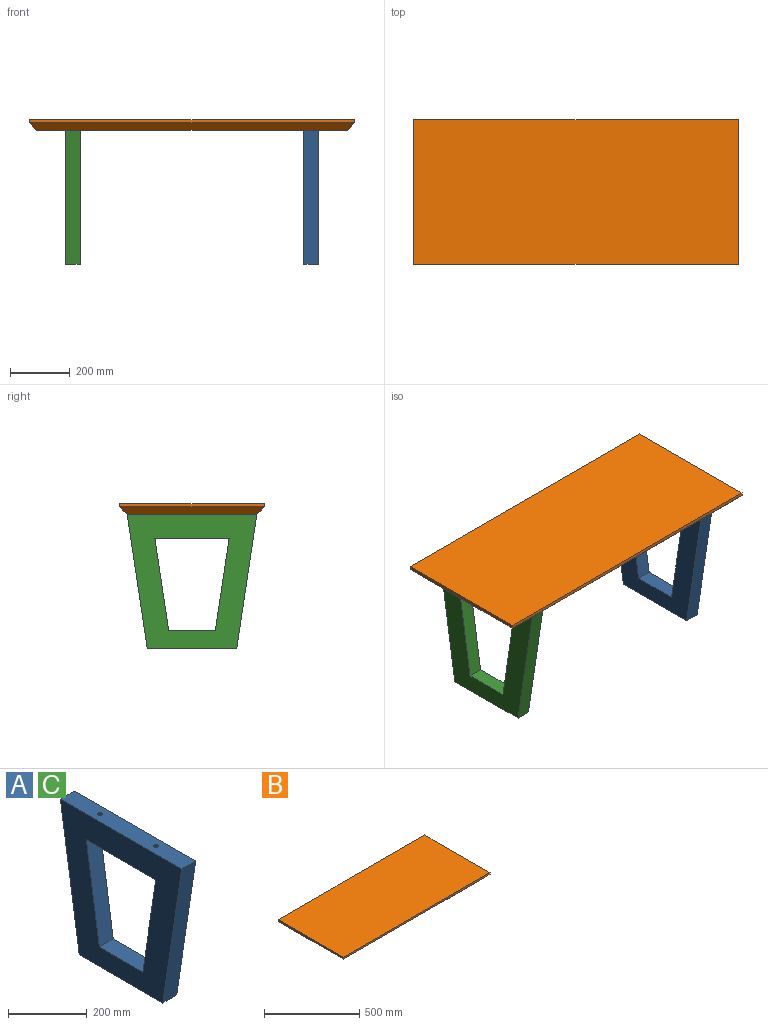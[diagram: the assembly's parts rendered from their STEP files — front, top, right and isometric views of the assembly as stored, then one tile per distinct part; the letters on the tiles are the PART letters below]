
ASSEMBLY  parts=3 mates=2
PART A: 16 faces, bbox 50x435x450 mm
  f0: cylinder r=6mm len=60mm, axis (0,0,-1), area 2261.9mm2, adj f5,f15
  f1: cylinder r=6mm len=60mm, axis (0,0,-1), area 2261.9mm2, adj f5,f13
  f2: plane 310x50mm, normal (0,0.99,0.15), area 15673.4mm2, adj f3,f9,f10,f11
  f3: plane 249.21x50mm, normal (0,0,-1), area 10536.3mm2, adj f2,f4,f10,f11,f12,f14
  f4: plane 310x50mm, normal (0,-0.99,0.15), area 15673.4mm2, adj f3,f9,f10,f11
  f5: plane 435x50mm, normal (0,0,1), area 21523.8mm2, adj f0,f1,f6,f8,f10,f11
  f6: plane 450x67.5mm, normal (0,-0.99,-0.15), area 22751.7mm2, adj f5,f7,f10,f11
  f7: plane 300x50mm, normal (0,0,-1), area 15000mm2, adj f6,f8,f10,f11
  f8: plane 450x67.5mm, normal (0,0.99,-0.15), area 22751.7mm2, adj f5,f7,f10,f11
  f9: plane 156.21x50mm, normal (0,0,1), area 7810.5mm2, adj f2,f4,f10,f11
  f10: plane 450x435mm, normal (1,0,0), area 102534.9mm2, adj f2,f3,f4,f5,f6,f7,f8,f9
  f11: plane 450x435mm, normal (-1,0,0), area 102534.9mm2, adj f2,f3,f4,f5,f6,f7,f8,f9
  f12: cylinder r=17.5mm len=35mm, axis (0,0,-1), area 2199.1mm2, adj f3,f13
  f13: plane 35x35mm, normal (0,0,-1), area 849mm2, adj f1,f12
  f14: cylinder r=17.5mm len=35mm, axis (0,0,-1), area 2199.1mm2, adj f3,f15
  f15: plane 35x35mm, normal (0,0,-1), area 849mm2, adj f0,f14
PART B: 10 faces, bbox 1090x485x36 mm
  f0: plane 485x11mm, normal (1,0,0), area 5335mm2, adj f1,f3,f4,f6
  f1: plane 1090x11mm, normal (0,1,0), area 11990mm2, adj f0,f2,f4,f7
  f2: plane 485x11mm, normal (-1,0,0), area 5335mm2, adj f1,f3,f4,f9
  f3: plane 1090x11mm, normal (0,-1,0), area 11990mm2, adj f0,f2,f4,f8
  f4: plane 1090x485mm, normal (0,0,1), area 528650mm2, adj f0,f1,f2,f3
  f5: plane 1040x435mm, normal (0,0,-1), area 452400mm2, adj f6,f7,f8,f9
  f6: plane 485x25mm, normal (0.71,0,-0.71), area 16263.5mm2, adj f0,f5,f7,f8
  f7: plane 1090x25mm, normal (0,0.71,-0.71), area 37653.4mm2, adj f1,f5,f6,f9
  f8: plane 1090x25mm, normal (0,-0.71,-0.71), area 37653.4mm2, adj f3,f5,f6,f9
  f9: plane 485x25mm, normal (-0.71,0,-0.71), area 16263.5mm2, adj f2,f5,f7,f8
PART C: same geometry as A
PLACE A t=(184.6,-243.08,-442.72)mm
PLACE B t=(-190.4,-93.08,7.28)mm
PLACE C t=(-615.4,-243.08,-442.72)mm
MATE fastened C.f5 <-> B.f5  axis (0,0,1) through (-590.4,-93.08,7.28)mm
MATE fastened A.f5 <-> B.f5  axis (0,0,1) through (209.6,-93.08,7.28)mm
